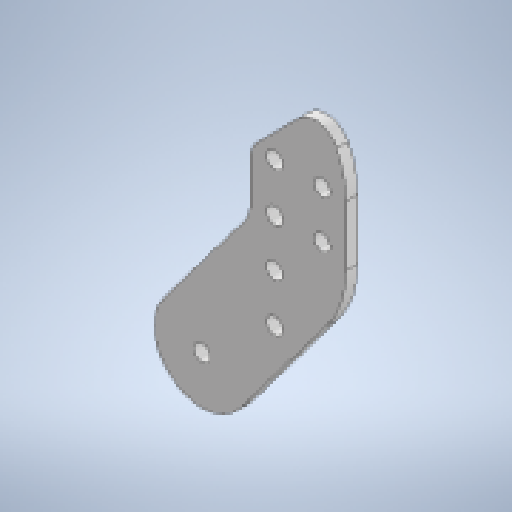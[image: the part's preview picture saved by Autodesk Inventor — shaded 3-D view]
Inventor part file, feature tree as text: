
AUTODESK INVENTOR PART (.ipt)
format: ipt  version: 2023 (Build 270158000, 158)  size: 175,104 bytes
history: native  units: in
note: dims shown in document units (in); Inventor stores cm internally (conversion verified against a paired STEP export)
features: extrude x1, fillet x1, sketch x1
ambient origin geometry x8: Origin, YZ Plane, XZ Plane, XY Plane, X Axis, Y Axis, Z Axis, Center Point
bodies: Solid1 (feature_tree)
feature tree (3):
  extrude  "Extrusion1"  Depth=1.0in
  fillet  "Fillet1"  Radius=1.5in
  sketch  "Sketch1"  dims[d0=0.17in d1=1.0in d2=1.5in d3=0.505in d4=0.625in d5=1.0in d6=45.0deg d7=0.17in d8=0.7874in d10=0.5in d11=0.7874in d13=0.5in d17=0.5in d18=0.5in d19=0.1181in d20=0.0in d21=0.25in]
